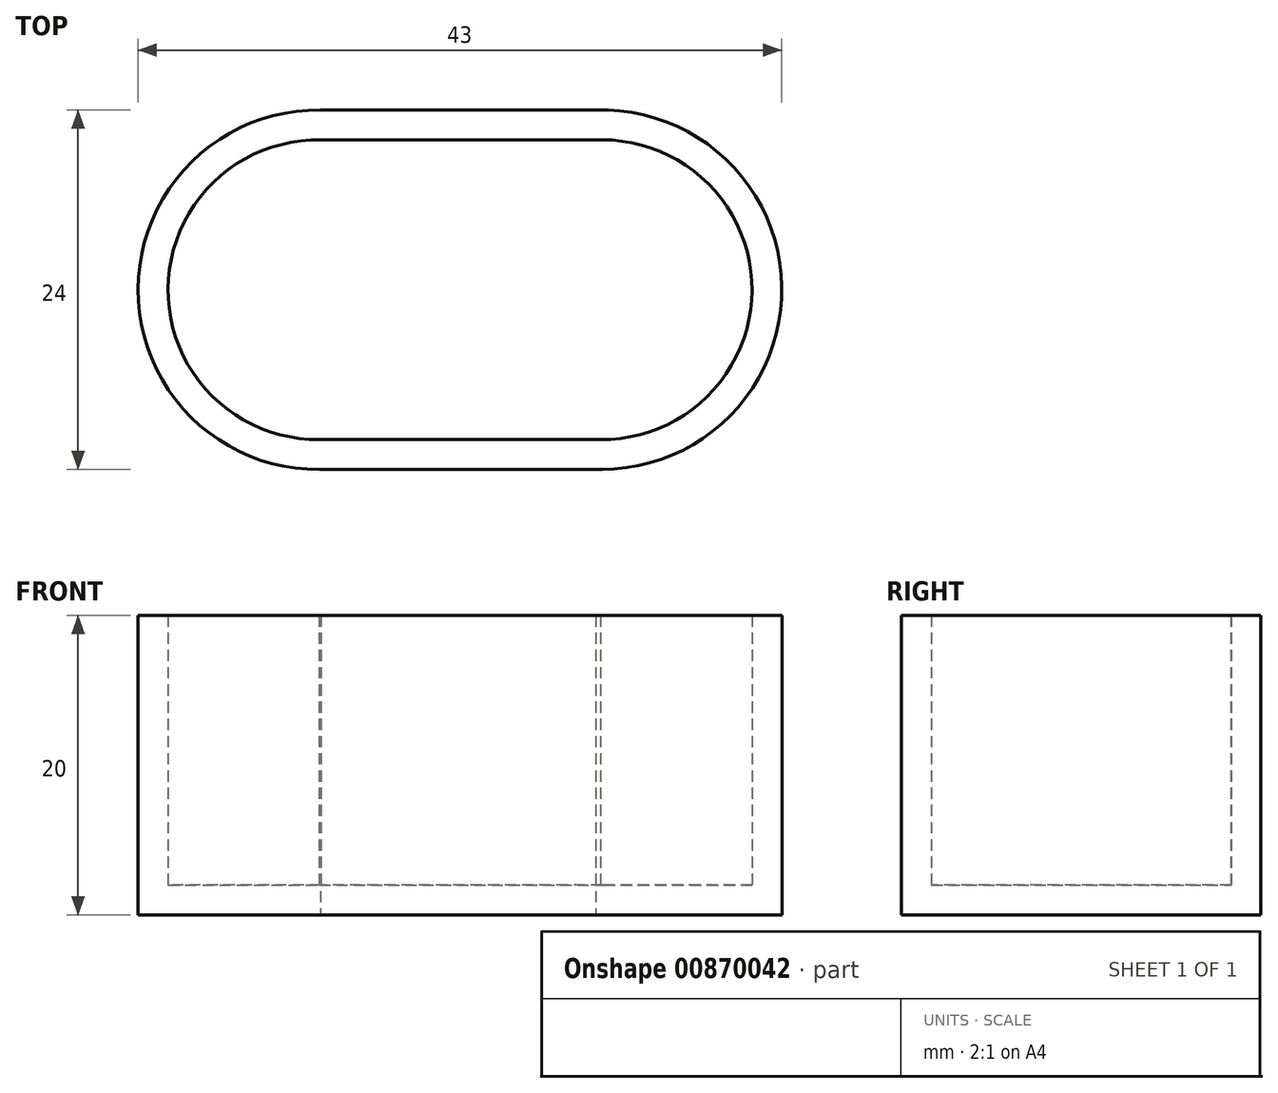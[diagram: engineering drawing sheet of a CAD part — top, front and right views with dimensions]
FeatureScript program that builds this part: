
annotation { "Feature Type Name" : "Feature", "Feature Type Description" : "" }
export const myFeature = defineFeature(function(context is Context, id is Id, definition is map)
    precondition{}
    {
        {
            var Q0;
            Q0=qCreatedBy(makeId("Top.planeOp"),FACE);
            var sketch = newSketch(context, id + "F0", { "sketchPlane" : qUnion([Q0])});
            skLineSegment(sketch, "E0", {"start": v(9.5, 10) * mm, "end": v(-9.71, 10) * mm});
            skLineSegment(sketch, "E1", {"start": v(9.61, -10) * mm, "end": v(-9.6, -10) * mm});
            skArc(sketch, "E2.trimOffspring", {"start": v(9.4, -10) * mm, "mid": v(19.5, -0.05) * mm, "end": v(9.5, 10) * mm});
            skArc(sketch, "E3.trimOffspring", {"start": v(-9.28, 10) * mm, "mid": v(-19.5, 0.05) * mm, "end": v(-9.39, -10) * mm});
            skArc(sketch, "E4", {"start": v(9.5, -12) * mm, "mid": v(21.5, 0.22) * mm, "end": v(9.08, 12) * mm});
            skLineSegment(sketch, "E5", {"start": v(-9.6, -12) * mm, "end": v(9.5, -12) * mm});
            skLineSegment(sketch, "E6", {"start": v(-9.68, 12) * mm, "end": v(9.93, 12) * mm});
            skArc(sketch, "E7.trimOffspring", {"start": v(-9.32, 12) * mm, "mid": v(-21.5, 0.03) * mm, "end": v(-9.39, -12) * mm});
            skSolve(sketch);
        }
        {
            var Q0;
            {var subQ0=sQuery(id+"F0.wireOp",EDGE,"E2.trimOffspring");var subQ6=sQuery(id+"F0.wireOp",EDGE,"E0");var subQ9=makeQuery(id+"F0.imprint","INTERSECT",VERTEX,{"derivedFrom":[subQ6,subQ0]});Q0=makeQuery(id+"F0.imprint","IMPRINT",FACE,{"disambiguationData":[TD([[makeQuery(id+"F0.imprint","IMPRINT",EDGE,{"disambiguationData":[TD([[subQ9,-1.0]])],"derivedFrom":subQ6}),1.0]])]});}
            extrude(context, id + "F1", {"entities" : qUnion([Q0]), "depth" : 2 * mm, "offsetDistance" : 25 * mm});
        }
        {
            var Q0;
            Q0 = qSketchRegion(id + "F0", true);
            extrude(context, id + "F2", {"entities" : qUnion([Q0]), "operationType" : NewBodyOperationType.ADD, "depth" : 20 * mm, "offsetDistance" : 25 * mm});
        }
    });
